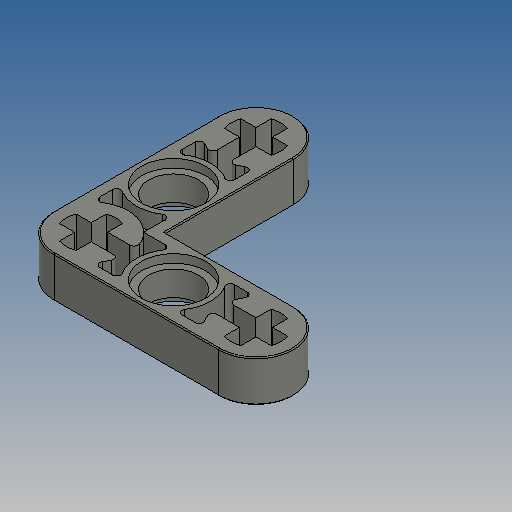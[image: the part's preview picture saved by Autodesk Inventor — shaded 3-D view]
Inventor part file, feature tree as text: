
AUTODESK INVENTOR PART (.ipt)
format: ipt  version: 2025 (Build 290162010, 162A)  size: 315,392 bytes
history: native  units: mm
features: extrude x3, sketch x2, mirror x1, fillet x1
ambient origin geometry x8: Origin, YZ Plane, XZ Plane, XY Plane, X Axis, Y Axis, Z Axis, Center Point
bodies: Solid1 (feature_tree)
feature tree (7):
  sketch  "Sketch1"  dims[d8=4.8mm d9=6.4mm]
  extrude  "Extrusion1"  Depth=6.4mm
  extrude  "Extrusion9"  Depth=7.2mm
  extrude  "Extrusion7"  Depth=8.0mm
  mirror  "Mirror1"
  fillet  "Fillet1"  Radius=0.8mm
  sketch  "Sketch6"  dims[d14=4.0mm d15=0.0mm d32=7.2mm d34=8.0mm d41=0.8mm d42=0.0mm d45=0.1mm d46=0.4mm d52=1.6mm d53=6.2mm d56=1.6mm d57=1.6mm d58=1.6mm d59=0.8mm d60=0.0mm]
